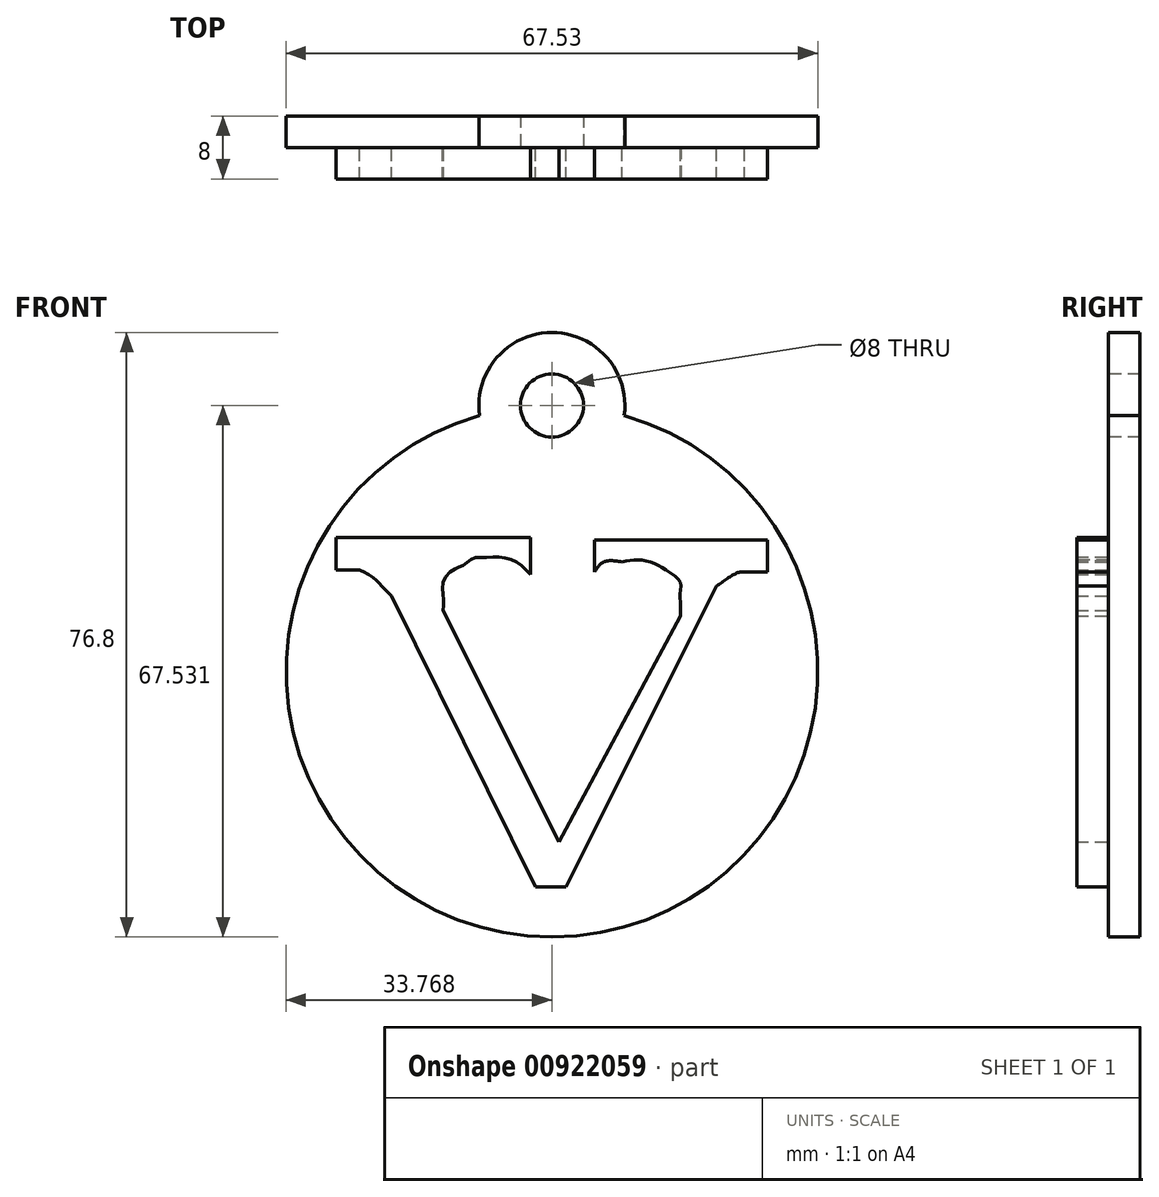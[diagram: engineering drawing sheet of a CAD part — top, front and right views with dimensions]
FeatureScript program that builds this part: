
annotation { "Feature Type Name" : "Feature", "Feature Type Description" : "" }
export const myFeature = defineFeature(function(context is Context, id is Id, definition is map)
    precondition{}
    {
        {
            var Q0;
            Q0=qCreatedBy(makeId("Front.planeOp"),FACE);
            var sketch = newSketch(context, id + "F0", { "sketchPlane" : qUnion([Q0])});
            skCircle(sketch, "E0", {"center": v(-5.4, 4.82) * mm, "radius": 33.76 * mm});
            skArc(sketch, "E1", {"start": v(3.78, 37.3) * mm, "mid": v(-5.4, 47.85) * mm, "end": v(-14.59, 37.3) * mm});
            skSolve(sketch);
        }
        {
            var Q0;
            Q0=qCreatedBy(makeId("Front.planeOp"),FACE);
            var sketch = newSketch(context, id + "F1", { "sketchPlane" : qUnion([Q0])});
            skLineSegment(sketch, "E2", {"start": v(-19.22, 12.53) * mm, "end": v(-4.48, -16.85) * mm});
            skLineSegment(sketch, "E3", {"start": v(-4.48, -16.85) * mm, "end": v(10.9, 11.87) * mm});
            skFitSpline(sketch, "E4", {"points": [v(-19.22, 12.53) * mm, v(-19.22, 14.22) * mm, v(-19.22, 16.2) * mm, v(-17.8, 17.79) * mm, v(-16.68, 18.26) * mm, v(-15.56, 19.1) * mm, v(-13.96, 19.3) * mm, v(-11.8, 19.3) * mm, v(-9.83, 18.63) * mm, v(-8.14, 17.13) * mm], "startDerivative": vector(0.78, 15.38) * mm, "endDerivative": vector(12.95, -13.5) * mm});
            skFitSpline(sketch, "E5", {"points": [v(10.9, 11.87) * mm, v(10.9, 13.65) * mm, v(10.9, 15.06) * mm, v(10.9, 16.19) * mm, v(9.31, 17.5) * mm, v(7.81, 18.44) * mm, v(6.22, 18.91) * mm, v(4.9, 18.91) * mm, v(3.5, 18.72) * mm], "startDerivative": vector(0.2, 13.67) * mm, "endDerivative": vector(-11.98, -1.8) * mm});
            skLineSegment(sketch, "E6", {"start": v(-8.14, 17.13) * mm, "end": v(-8.14, 21.82) * mm});
            skLineSegment(sketch, "E7", {"start": v(-8.14, 21.82) * mm, "end": v(-32.82, 21.82) * mm});
            skLineSegment(sketch, "E8", {"start": v(-32.82, 21.82) * mm, "end": v(-32.82, 17.7) * mm});
            skLineSegment(sketch, "E9", {"start": v(-32.82, 17.7) * mm, "end": v(-29.82, 17.7) * mm});
            skFitSpline(sketch, "E10", {"points": [v(-29.82, 17.7) * mm, v(-28.13, 16.75) * mm, v(-27.1, 15.72) * mm, v(-25.78, 14.4) * mm], "startDerivative": vector(5.25, -2.5) * mm, "endDerivative": vector(4.03, -3.9) * mm});
            skLineSegment(sketch, "E11", {"start": v(-25.78, 14.4) * mm, "end": v(-7.49, -22.57) * mm});
            skLineSegment(sketch, "E12", {"start": v(-7.49, -22.57) * mm, "end": v(-3.64, -22.57) * mm});
            skLineSegment(sketch, "E13", {"start": v(-3.64, -22.57) * mm, "end": v(15.5, 15.63) * mm});
            skFitSpline(sketch, "E14", {"points": [v(15.5, 15.63) * mm, v(17.1, 16.75) * mm, v(18.42, 17.4) * mm, v(19.07, 17.4) * mm], "startDerivative": vector(3.88, 2.86) * mm, "endDerivative": vector(2.58, -0.35) * mm});
            skLineSegment(sketch, "E15", {"start": v(19.07, 17.4) * mm, "end": v(21.95, 17.4) * mm});
            skLineSegment(sketch, "E16", {"start": v(21.95, 17.4) * mm, "end": v(21.95, 17.4) * mm});
            skLineSegment(sketch, "E17", {"start": v(21.95, 17.4) * mm, "end": v(21.95, 21.5) * mm});
            skLineSegment(sketch, "E18", {"start": v(21.95, 21.5) * mm, "end": v(0, 21.5) * mm});
            skLineSegment(sketch, "E19", {"start": v(0, 21.5) * mm, "end": v(0, 17.4) * mm});
            skFitSpline(sketch, "E20", {"points": [v(0, 17.4) * mm, v(1.2, 18.72) * mm, v(3.5, 18.72) * mm], "startDerivative": vector(2.17, 3.46) * mm, "endDerivative": vector(4.77, -0.74) * mm});
            skSolve(sketch);
        }
        {
            var Q0;
            Q0 = qSketchRegion(id + "F0", true);
            extrude(context, id + "F2", {"entities" : qUnion([Q0]), "depth" : 4 * mm, "offsetDistance" : 25 * mm});
        }
        {
            var Q0;
            Q0 = qSketchRegion(id + "F1", true);
            extrude(context, id + "F3", {"entities" : qUnion([Q0]), "operationType" : NewBodyOperationType.ADD, "depth" : 8 * mm, "offsetDistance" : 25 * mm});
        }
        {
            var Q0;
            Q0=sQuery(id+"F0.wireOp",VERTEX,"E1.center");
            var Q1;
            Q1=makeQuery(id+"F2.opExtrude","SWEPT_BODY",BODY,{"disambiguationData":[OSD([sQuery(id+"F0.wireOp",EDGE,"E0"),sQuery(id+"F0.wireOp",EDGE,"E1")])]});
            hole(context, id + "F4", {"style" : HoleStyle.SIMPLE, "endStyle" : HoleEndStyle.THROUGH, "oppositeDirection" : true, "holeDiameter" : 8 * mm, "majorDiameter" : 5 * mm, "isTappedThrough" : true, "tappedDepth" : 12 * mm, "tapClearance" : 3, "locations" : qUnion([Q0]), "scope" : qUnion([Q1])});
        }
    });
